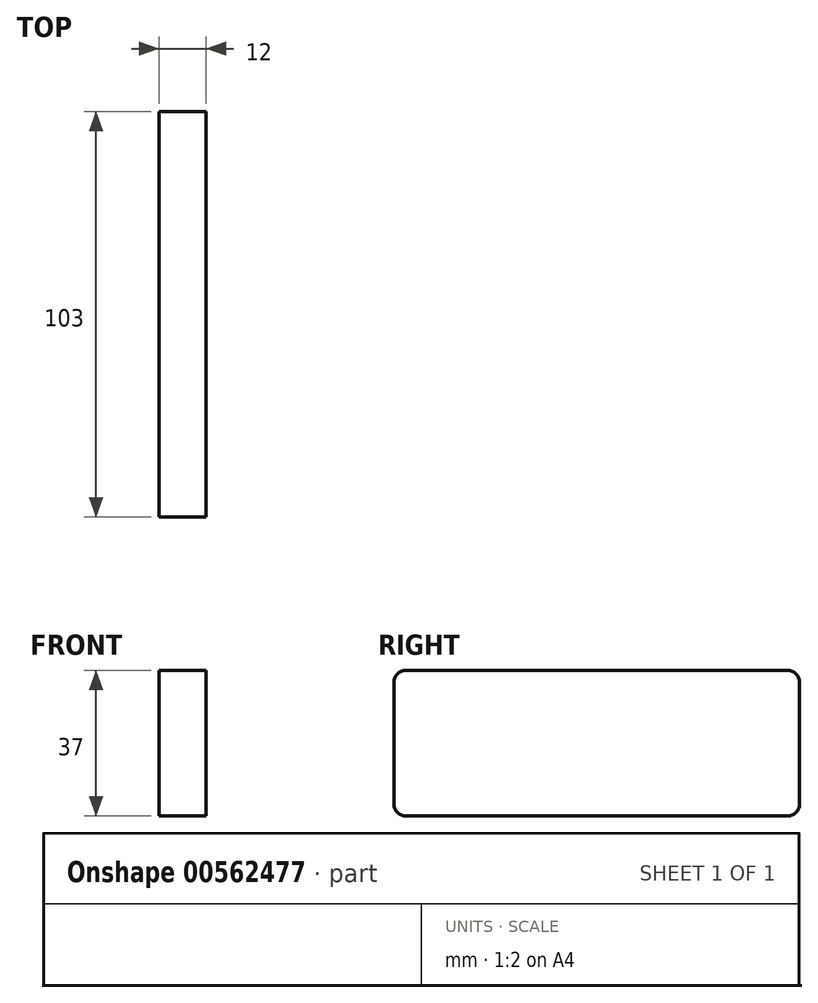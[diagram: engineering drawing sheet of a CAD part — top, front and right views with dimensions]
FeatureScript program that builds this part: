
annotation { "Feature Type Name" : "Feature", "Feature Type Description" : "" }
export const myFeature = defineFeature(function(context is Context, id is Id, definition is map)
    precondition{}
    {
        {
            var Q0;
            Q0=qCreatedBy(makeId("Right.planeOp"),FACE);
            var sketch = newSketch(context, id + "F0", { "sketchPlane" : qUnion([Q0])});
            skLineSegment(sketch, "E0.bottom", {"start": v(-51.5, 18.5) * mm, "end": v(51.5, 18.5) * mm});
            skLineSegment(sketch, "E0.top", {"start": v(-51.5, -18.5) * mm, "end": v(51.5, -18.5) * mm});
            skLineSegment(sketch, "E0.left", {"start": v(-51.5, 18.5) * mm, "end": v(-51.5, -18.5) * mm});
            skLineSegment(sketch, "E0.right", {"start": v(51.5, 18.5) * mm, "end": v(51.5, -18.5) * mm});
            skPoint(sketch, "E0.middle", {"position": v(0, 0) * mm});
            skSolve(sketch);
        }
        {
            var Q0;
            Q0=makeQuery(id+"F0.imprint","IMPRINT",FACE,{"disambiguationData":[TD([[makeQuery(id+"F0.imprint","IMPRINT",EDGE,{"derivedFrom":sQuery(id+"F0.wireOp",EDGE,"E0.bottom")}),-1.0]])]});
            extrude(context, id + "F1", {"entities" : qUnion([Q0]), "depth" : 12 * mm, "offsetDistance" : 25 * mm, "symmetric" : true});
        }
        {
            var Q0;
            Q0=makeQuery(id+"F1.opExtrude","SWEPT_EDGE",EDGE,{"disambiguationData":[OSD([sQuery(id+"F0.wireOp",EDGE,"E0.bottom"),sQuery(id+"F0.wireOp",EDGE,"E0.left")])]});
            var Q1;
            Q1=makeQuery(id+"F1.opExtrude","SWEPT_EDGE",EDGE,{"disambiguationData":[OSD([sQuery(id+"F0.wireOp",EDGE,"E0.top"),sQuery(id+"F0.wireOp",EDGE,"E0.left")])]});
            var Q2;
            Q2=makeQuery(id+"F1.opExtrude","SWEPT_EDGE",EDGE,{"disambiguationData":[OSD([sQuery(id+"F0.wireOp",EDGE,"E0.top"),sQuery(id+"F0.wireOp",EDGE,"E0.right")])]});
            var Q3;
            Q3=makeQuery(id+"F1.opExtrude","SWEPT_EDGE",EDGE,{"disambiguationData":[OSD([sQuery(id+"F0.wireOp",EDGE,"E0.bottom"),sQuery(id+"F0.wireOp",EDGE,"E0.right")])]});
            fillet(context, id + "F2", {"entities" : qUnion([Q0, Q1, Q2, Q3]), "radius" : 3 * mm, "tangentPropagation" : true, "allowEdgeOverflow" : false});
        }
    });
